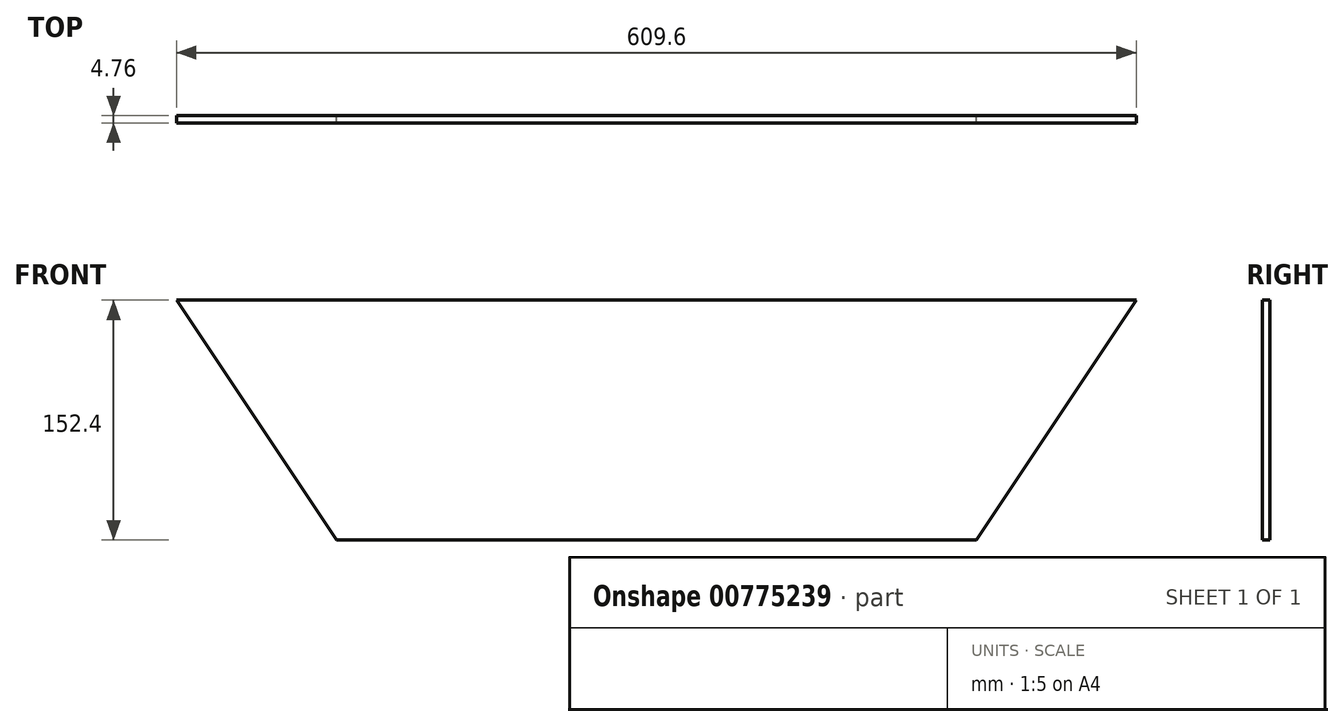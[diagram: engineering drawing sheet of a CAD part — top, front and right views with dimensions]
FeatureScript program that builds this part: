
annotation { "Feature Type Name" : "Feature", "Feature Type Description" : "" }
export const myFeature = defineFeature(function(context is Context, id is Id, definition is map)
    precondition{}
    {
        {
            var Q0;
            Q0=qCreatedBy(makeId("Front.planeOp"),FACE);
            var sketch = newSketch(context, id + "F0", { "sketchPlane" : qUnion([Q0])});
            skLineSegment(sketch, "E0.top", {"start": v(203.2, -118.71) * mm, "end": v(-203.2, -118.71) * mm});
            skPoint(sketch, "E0.middle", {"position": v(0, 0) * mm});
            skLineSegment(sketch, "E1.bottom", {"start": v(304.8, 33.69) * mm, "end": v(-304.8, 33.69) * mm});
            skLineSegment(sketch, "E2", {"start": v(-304.8, 33.69) * mm, "end": v(-203.2, -118.71) * mm});
            skLineSegment(sketch, "E3", {"start": v(304.8, 33.69) * mm, "end": v(203.2, -118.71) * mm});
            skSolve(sketch);
        }
        {
            var Q0;
            Q0=makeQuery(id+"F0.imprint","IMPRINT",FACE,{"disambiguationData":[TD([[makeQuery(id+"F0.imprint","IMPRINT",EDGE,{"derivedFrom":sQuery(id+"F0.wireOp",EDGE,"E0.top")}),-1.0]])]});
            extrude(context, id + "F1", {"entities" : qUnion([Q0]), "endBound" : BoundingType.SYMMETRIC, "depth" : 4.76 * mm, "offsetDistance" : 25.4 * mm});
        }
    });
